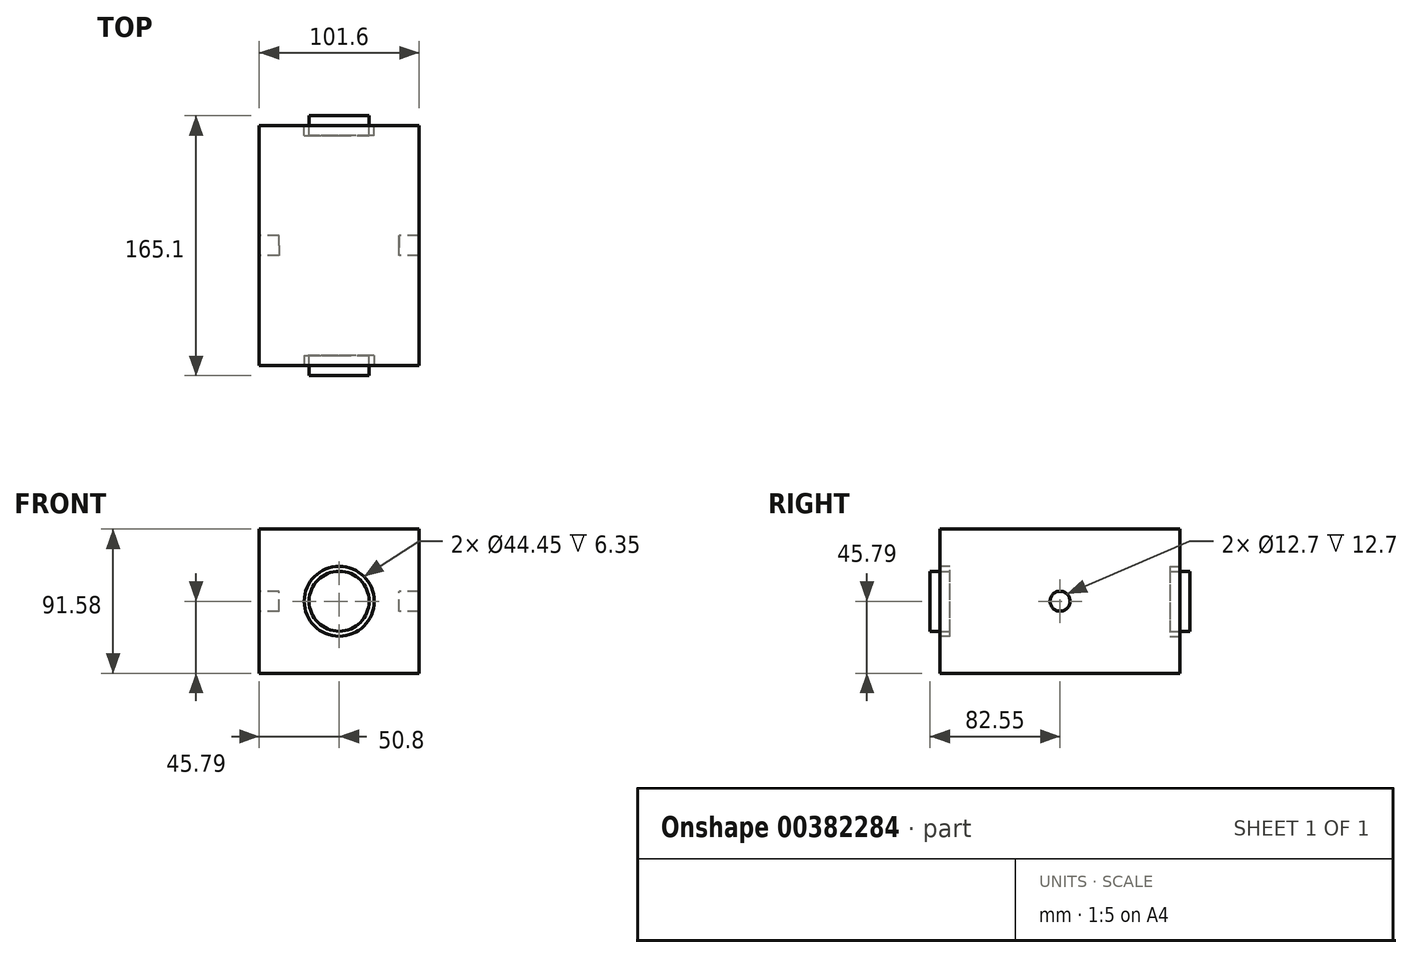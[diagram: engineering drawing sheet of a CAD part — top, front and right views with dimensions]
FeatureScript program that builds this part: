
annotation { "Feature Type Name" : "Feature", "Feature Type Description" : "" }
export const myFeature = defineFeature(function(context is Context, id is Id, definition is map)
    precondition{}
    {
        {
            var Q0;
            Q0=qCreatedBy(makeId("Right.planeOp"),FACE);
            var sketch = newSketch(context, id + "F0", { "sketchPlane" : qUnion([Q0])});
            skCircle(sketch, "E0", {"center": v(0, 0) * mm, "radius": 101.6 * mm});
            skCircle(sketch, "E1.0", {"center": v(0, 0) * mm, "radius": 88.9 * mm});
            skLineSegment(sketch, "E2.bottom", {"start": v(76.2, -45.8) * mm, "end": v(-76.2, -45.8) * mm});
            skLineSegment(sketch, "E2.top", {"start": v(76.2, 45.8) * mm, "end": v(-76.2, 45.8) * mm});
            skLineSegment(sketch, "E2.left", {"start": v(76.2, -45.8) * mm, "end": v(76.2, 45.8) * mm});
            skLineSegment(sketch, "E2.right", {"start": v(-76.2, -45.8) * mm, "end": v(-76.2, 45.8) * mm});
            skSolve(sketch);
        }
        {
            var Q0;
            Q0=makeQuery(id+"F0.imprint","IMPRINT",FACE,{"disambiguationData":[TD([[makeQuery(id+"F0.imprint","IMPRINT",EDGE,{"derivedFrom":sQuery(id+"F0.wireOp",EDGE,"E2.bottom")}),-1.0]])]});
            extrude(context, id + "F1", {"entities" : qUnion([Q0]), "endBound" : BoundingType.SYMMETRIC, "depth" : 101.6 * mm});
        }
        {
            var Q0;
            Q0=makeQuery(id+"F1.opExtrude","SWEPT_FACE",FACE,{"disambiguationData":[OSD([sQuery(id+"F0.wireOp",EDGE,"E2.right")])]});
            var sketch = newSketch(context, id + "F2", { "sketchPlane" : qUnion([Q0])});
            skCircle(sketch, "E3", {"center": v(0, 0) * mm, "radius": 22.23 * mm});
            skCircle(sketch, "E4.0", {"center": v(0, 0) * mm, "radius": 19.05 * mm});
            skSolve(sketch);
        }
        {
            var Q0;
            Q0=makeQuery(id+"F2.imprint","IMPRINT",FACE,{"disambiguationData":[TD([[makeQuery(id+"F2.imprint","IMPRINT",EDGE,{"derivedFrom":sQuery(id+"F2.wireOp",EDGE,"E4.0")}),1.0]])]});
            extrude(context, id + "F3", {"entities" : qUnion([Q0]), "operationType" : NewBodyOperationType.REMOVE, "endBound" : BoundingType.SYMMETRIC, "oppositeDirection" : true, "depth" : 304.8 * mm});
        }
        {
            var Q0;
            Q0=makeQuery(id+"F2.imprint","IMPRINT",FACE,{"disambiguationData":[TD([[makeQuery(id+"F2.imprint","IMPRINT",EDGE,{"derivedFrom":sQuery(id+"F2.wireOp",EDGE,"E3")}),1.0]])]});
            extrude(context, id + "F4", {"entities" : qUnion([Q0]), "operationType" : NewBodyOperationType.REMOVE, "oppositeDirection" : true, "depth" : 6.35 * mm});
        }
        {
            var Q0;
            Q0=makeQuery(id+"F1.opExtrude","SWEPT_FACE",FACE,{"disambiguationData":[OSD([sQuery(id+"F0.wireOp",EDGE,"E2.left")])]});
            var sketch = newSketch(context, id + "F5", { "sketchPlane" : qUnion([Q0])});
            skCircle(sketch, "E5", {"center": v(0, 0) * mm, "radius": 22.23 * mm});
            skCircle(sketch, "E6", {"center": v(0, 0) * mm, "radius": 19.05 * mm});
            skSolve(sketch);
        }
        {
            var Q0;
            Q0=makeQuery(id+"F5.imprint","IMPRINT",FACE,{"disambiguationData":[TD([[makeQuery(id+"F5.imprint","IMPRINT",EDGE,{"derivedFrom":sQuery(id+"F5.wireOp",EDGE,"E5")}),1.0]])]});
            extrude(context, id + "F6", {"entities" : qUnion([Q0]), "operationType" : NewBodyOperationType.REMOVE, "oppositeDirection" : true, "depth" : 6.35 * mm});
        }
        {
            var Q0;
            Q0=qCreatedBy(makeId("Front.planeOp"),FACE);
            var sketch = newSketch(context, id + "F7", { "sketchPlane" : qUnion([Q0])});
            skCircle(sketch, "E7", {"center": v(0, 0) * mm, "radius": 19.05 * mm});
            skSolve(sketch);
        }
        {
            var Q0;
            Q0 = qSketchRegion(id + "F7", true);
            extrude(context, id + "F8", {"entities" : qUnion([Q0]), "operationType" : NewBodyOperationType.ADD, "endBound" : BoundingType.SYMMETRIC, "depth" : 165.1 * mm});
        }
        {
            var Q0;
            Q0=makeQuery(id+"F8.opExtrude","CAP_FACE",FACE,{"disambiguationData":[OSD([sQuery(id+"F7.wireOp",EDGE,"E7")])],"isStart":false});
            var sketch = newSketch(context, id + "F9", { "sketchPlane" : qUnion([Q0])});
            skSolve(sketch);
        }
        {
            var Q0;
            Q0=makeQuery(id+"F1.opExtrude","CAP_FACE",FACE,{"disambiguationData":[OSD([sQuery(id+"F0.wireOp",EDGE,"E2.bottom"),sQuery(id+"F0.wireOp",EDGE,"E2.top"),sQuery(id+"F0.wireOp",EDGE,"E2.left"),sQuery(id+"F0.wireOp",EDGE,"E2.right")])],"isStart":true});
            var sketch = newSketch(context, id + "F10", { "sketchPlane" : qUnion([Q0])});
            skCircle(sketch, "E8", {"center": v(0, 0) * mm, "radius": 6.35 * mm});
            skSolve(sketch);
        }
        {
            var Q0;
            Q0=makeQuery(id+"F10.imprint","IMPRINT",FACE,{"disambiguationData":[TD([[makeQuery(id+"F10.imprint","IMPRINT",EDGE,{"derivedFrom":sQuery(id+"F10.wireOp",EDGE,"E8")}),1.0]])]});
            extrude(context, id + "F11", {"entities" : qUnion([Q0]), "operationType" : NewBodyOperationType.REMOVE, "oppositeDirection" : true, "depth" : 152.4 * mm});
        }
        {
            var Q0;
            Q0=qCreatedBy(makeId("Right.planeOp"),FACE);
            var sketch = newSketch(context, id + "F12", { "sketchPlane" : qUnion([Q0])});
            skCircle(sketch, "E9", {"center": v(0, 0) * mm, "radius": 6.35 * mm});
            skSolve(sketch);
        }
        {
            var Q0;
            Q0 = qSketchRegion(id + "F12", true);
            extrude(context, id + "F13", {"entities" : qUnion([Q0]), "operationType" : NewBodyOperationType.ADD, "endBound" : BoundingType.SYMMETRIC, "depth" : 76.2 * mm});
        }
    });
